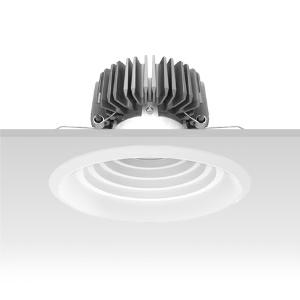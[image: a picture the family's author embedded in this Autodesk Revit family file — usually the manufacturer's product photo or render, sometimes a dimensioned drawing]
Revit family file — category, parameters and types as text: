
# Revit family: 3f_filippi_-_3f_reno_bianco_ampio_3f_filippi_-_30691_-_3f_reno_200_wh_4000-930_dali_wide
name_source: partatom
category: Lighting Fixtures
units: mm (PartAtom-declared; Revit-internal decimal feet)

## family parameters
Cut with Voids When Loaded = No
Host = Face
Light Source = No
Part Type = Normal
Room Calculation Point = No
Round Connector Dimension = Use Diameter
Shared = No

## types (1)
- 3F Filippi - 3F Reno Bianco Ampio (1 x LED, 3192 lm, 43 W, 3000 K)
    Apparent Load = 43 VA
    Approval mark = CE
    CIE Flux Codes = 80 97 100 100 100
    Color Rendering = 90
    Color Temperature = 3000 K
    Control Gear = Electronic transformer
    Default Elevation = 1800 mm
    Description = ILLUMINOTECHNICAL
Luminous efficiency 100% (DLOR 100%, ULOR 0%).
Initial luminous flux of the luminaire 3192 lm.
Direct symmetric wide distribution.
Installation Interdistance Transv.D = 1.56 x hu - Long.D = 1.56 x hu.
Tabular UGR (CIE 117 - 4H-8H; S=0.25H; 70/50/20): RUG 21 - 21.
Beam angle: 85° - 84°.
Luminous efficacy 74 lm/W.
Lifetime (L90/B10): 30000 h. (tq+25°C)
Lifetime (L85/B10): 50000 h. (tq+25°C)
Lifetime (L70/B10): 80000 h. (tq+25°C)
Sudden decreased luminous flux after 50000 hours: 0% (C0).
Photobiological safety in compliance with IEC/TR 62778: RG1 low risk, (IEC 62471).
In compliance with IEC/EN 62722-2-1 - IEC/EN 62717 standards.

SOURCE
Compact LED module 4000/930.
Energy efficiency class (UE 2019/2020 - UE 2019/2015): F.
CIE 13.3 Colour rendering index: CRI >90 (R9 >50%).
IES TM-30 Fidelity Index: Rf = 92 Rg = 101.
CCT nominal colour temperature 3000 K.
Colour initial tolerance (MacAdam): SDCM 3.
Zhaga Book 3 compliant.

MECHANICAL
Passive heat dissipator in die-casting aluminium, oversized, for optimum thermal management of the LED module.
Parabolic element with graduated/concentric rings in white polycarbonate.
Transparent external lens with glossy and satin differentiated surfaces, with a cooling and anti-insect system in methacrylate (PMMA).
Fastening spring clips in stainless steel.
Dimensions: diameter 216 mm, height 142 mm. Weight 1.525 kg.
IP44 protection degree for exposed part, IP20 for recessed part.
Mechanical strength to impacts IK04 (0.5 joule).
Glow-wire test resistance 650°C.

ELECTRICAL
Wiring on a separate unit.
Halogen Free DALI-2 DATI (Parts 251, 252, 253), PUSH-DIM, electronic wiring 230V-50/60Hz, power factor 0.97 at full load, THD <25%, constant output current, SELV, class II, 1 driver, 1 DALI addresse.
Power of the luminaire 43 W.
ENEC - CE.
SAFE FLICKER: PstLM=<1 and SVM=<0.4 (IEC TR 61547-1 and IEC TR 63158), to ensure a more comfortable and safe light.
Luminaire compliant with EN 60598-2-22 for power supply from a centralised emergency system CPSS (Central Power Supply System), not incorporated in the luminaire - high risk areas excluded. The default power and flux are 100% in AC and 100% in DC.
Ambient temperature from 0°C to +25°C.
Temperature class T6 max 85°C.
Relative humidity UR: <85%.

INSTALLATION
Pull-up recessed fitting.
False ceiling carving: 200 mm.
All accessories dedicated to this product are available on the Catalog and on our website www.3F-Filippi.com.

APPLICATIONS
Environments: architectural, commercial, exhibition areas, transit areas, corridors, shops, display windows, service areas.
In false ceilings with narrow voids.

LIGHT MANAGEMENT
Recommended minimum setting: 10%.
The luminaire, equipped with (DALI-2 DATI) driver, can be controlled manually with 3F Easy Dim technology or automatically/manually with wired or wireless DALI/D2D control systems.
The D2D driver guarantees interoperability with other devices with the same certification by making the following information available:
Device Data (Part 251), Energy Report (Part 252), Diagnosis & Maintenance (Part 253).
In electrical systems without a regulation system (manual or automatic) and DALI bus, a suitable jumper must be made on the DA-DA terminals of the appliance.

WARNING
Luminaire designed for disposal/recycling at end-of-life.
Replaceable (LED only) light source by a professional. Replaceable control gear by a professional.
    Height = 0 mm  [stored 0 ft]
    Lamp = 1 x LED
    Lamp Light Flux = 3192 lm
    Lamp Power = 43 W
    Lamp count = 1
    Length = 216 mm
    Lifetime = 50000 h
    Luminous efficacy = 74 lm/W
    Manufacturer = 3F Filippi
    ModVariant = No
    Model = 3F Filippi - 30691 - 3F Reno 200 WH 4000-930 DALI WIDE
    Mounting Place = Ceiling
    Mounting Type = Recessed
    Number of Poles = 1
    OnlyDefault = Yes
    Power Factor = 1
    Product Name = 3F Filippi - 3F Reno Bianco Ampio
    Product group = recessed luminaire
    ProductGroupID = 4
    Protection Class = Protection class II
    Protection Degree = IP 20
    RLX_Detail_Level = 1
    RLX_Emergency_Light_Flux = 0 lm
    RLX_Emergency_Type = 0
    RLX_Emergency_Type_DB = No
    RlxData = <blob elided: 93809 chars, md5=90365649>
    Socket = socket
    Standby Power = 0 W
    System Light Flux = 3192 lm
    System Power = 43 W
    Type Comments = Product without accessories
    Type Image = 3ffilippi_3f_reno_200_wh_2500_3000_4000.jpg
    URL = http://relux.com
    VarID = ---
    Voltage = 0 V
    Weight = 0.00 kg
    Width = 0 mm  [stored 0 ft]

note: [stored X ft] marks values corroborated as IEEE doubles in the binary element streams (Revit-internal decimal feet)

## geometry (parser evidence)
native form markers: Blend x4, Sweep x9
no freeform markers — native parametric forms only
